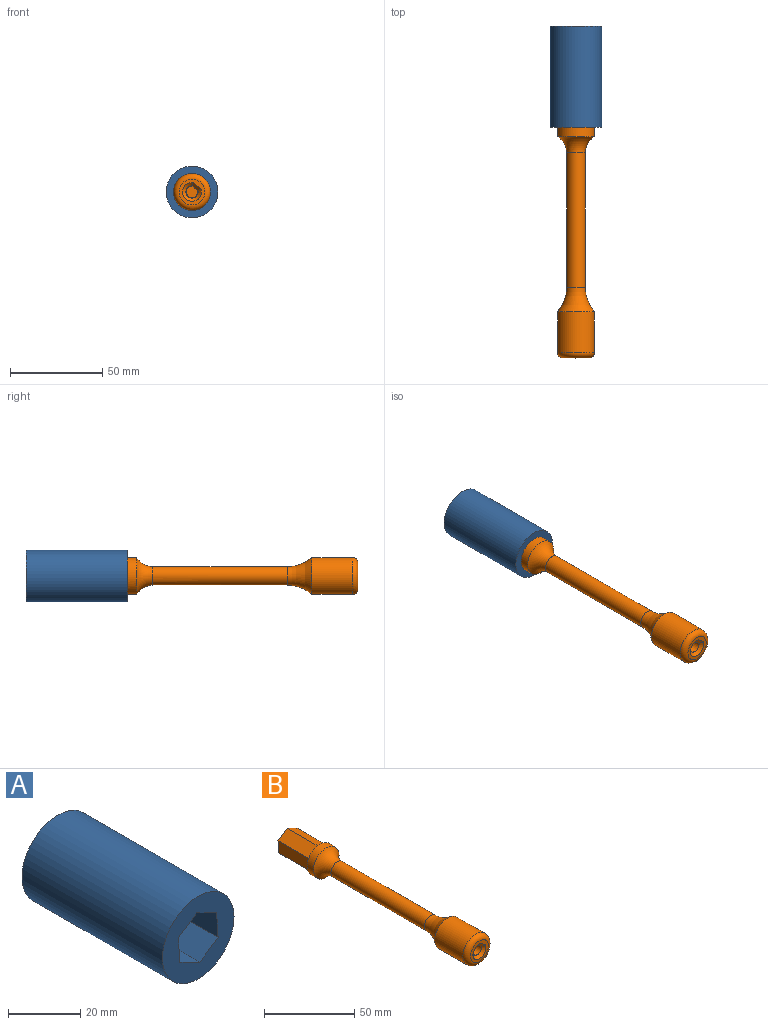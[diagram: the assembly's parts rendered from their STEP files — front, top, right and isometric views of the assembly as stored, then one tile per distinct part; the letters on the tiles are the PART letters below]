
ASSEMBLY  parts=2 mates=1
PART A: 11 faces, bbox 28x55x28 mm
  f0: cylinder r=6mm len=30mm, axis (0,1,0), area 1131mm2, adj f3,f10
  f1: plane 28x28mm, normal (0,-1,0), area 420.9mm2, adj f2,f4,f5,f6,f7,f8,f9
  f2: cylinder r=14mm len=55mm, axis (0,1,0), area 4838.1mm2, adj f1,f3
  f3: plane 28x28mm, normal (0,1,0), area 502.7mm2, adj f0,f2
  f4: plane 25x7.78mm, normal (0.44,0,0.9), area 216.5mm2, adj f1,f5,f9,f10
  f5: plane 25x7.18mm, normal (-0.56,0,0.83), area 216.5mm2, adj f1,f4,f6,f10
  f6: plane 25x8.64mm, normal (-1,0,-0.07), area 216.5mm2, adj f1,f5,f7,f10
  f7: plane 25x7.78mm, normal (-0.44,0,-0.9), area 216.5mm2, adj f1,f6,f8,f10
  f8: plane 25x7.18mm, normal (0.56,0,-0.83), area 216.5mm2, adj f1,f7,f9,f10
  f9: plane 25x8.64mm, normal (1,0,0.07), area 216.5mm2, adj f1,f4,f8,f10
  f10: plane 17.28x15.56mm, normal (0,-1,0), area 81.8mm2, adj f0,f4,f5,f6,f7,f8,f9
PART B: 20 faces, bbox 32.6x150.1x32.6 mm
  f0: cylinder r=5mm len=73.11mm, axis (0,1,0), area 2296.8mm2, adj f10,f16
  f1: plane 20x20mm, normal (0,1,0), area 119.3mm2, adj f2,f4,f5,f6,f7,f8,f9
  f2: cylinder r=10mm len=20mm, axis (0,1,0), area 314.2mm2, adj f1,f10
  f3: plane 17.28x15.56mm, normal (0,1,0), area 194.9mm2, adj f4,f5,f6,f7,f8,f9
  f4: plane 25x8.64mm, normal (1,0,0.07), area 216.5mm2, adj f1,f3,f5,f9
  f5: plane 25x7.18mm, normal (0.56,0,-0.83), area 216.5mm2, adj f1,f3,f4,f6
  f6: plane 25x7.78mm, normal (-0.44,0,-0.9), area 216.5mm2, adj f1,f3,f5,f7
  f7: plane 25x8.64mm, normal (-1,0,-0.07), area 216.5mm2, adj f1,f3,f6,f8
  f8: plane 25x7.18mm, normal (-0.56,0,0.83), area 216.5mm2, adj f1,f3,f7,f9
  f9: plane 25x7.78mm, normal (0.44,0,0.9), area 216.5mm2, adj f1,f3,f4,f8
  f10: torus R=15mm, axis (0,1,0), area 442.8mm2, adj f0,f2
  f11: cone r=3.1mm half-angle=0.5deg, axis (0,-1,0), area 367.3mm2, adj f12,f15,f18
  f12: plane 23.2x3.23mm, normal (-0.62,-0.01,-0.78), area 92.1mm2, adj f11,f15,f19
  f13: cylinder r=10mm len=22mm, axis (0,1,0), area 1382.3mm2, adj f16,f17
  f14: plane 14x14mm, normal (0,-1,0), area 74.6mm2, adj f17,f18,f19
  f15: plane 6.2x6.2mm, normal (0,-1,0), area 28.4mm2, adj f11,f12
  f16: torus R=25mm, axis (0,-1,0), area 608.2mm2, adj f0,f13
  f17: torus R=7mm, axis (0,-1,0), area 263.8mm2, adj f13,f14
  f18: cone r=3.1mm half-angle=45deg, axis (0,-1,0), area 54.6mm2, adj f11,f14,f19
  f19: plane 4.8x4.35mm, normal (-0.44,-0.71,-0.55), area 11.7mm2, adj f12,f14,f18
PLACE A t=(-12.96,-14.93,35.07)mm
PLACE B t=(-12.96,35.07,35.07)mm
MATE slider B.f11 <-> A.f0  axis (0,-1,0) through (-12.96,-44.93,35.07)mm
